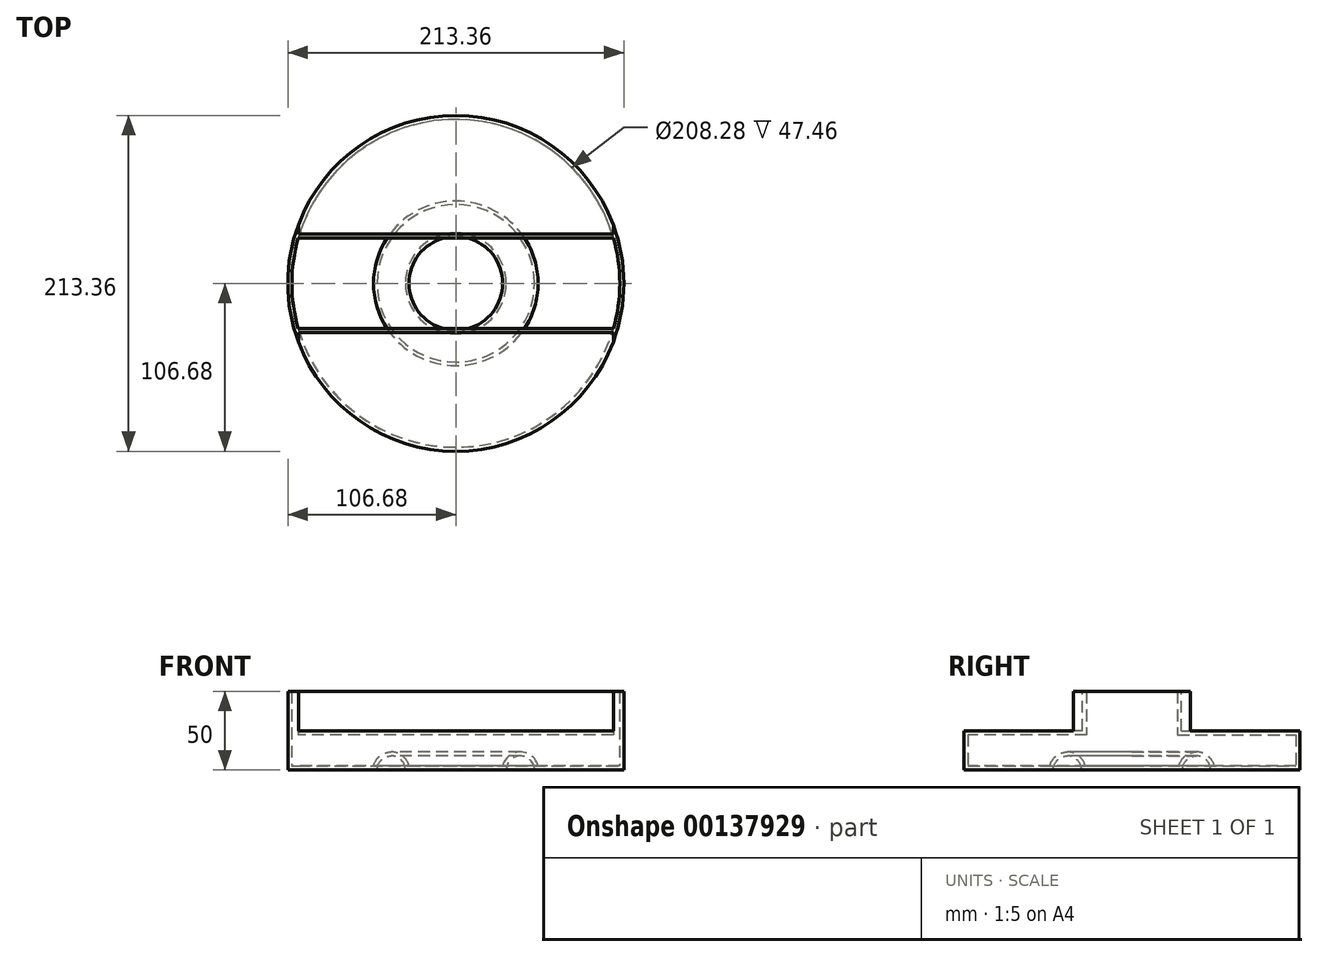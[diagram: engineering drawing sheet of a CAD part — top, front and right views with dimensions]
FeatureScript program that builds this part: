
annotation { "Feature Type Name" : "Feature", "Feature Type Description" : "" }
export const myFeature = defineFeature(function(context is Context, id is Id, definition is map)
    precondition{}
    {
        {
            var Q0;
            Q0=qCreatedBy(makeId("Top.planeOp"),FACE);
            var sketch = newSketch(context, id + "F0", { "sketchPlane" : qUnion([Q0])});
            skCircle(sketch, "E0", {"center": v(0, 0) * mm, "radius": 106.68 * mm});
            skSolve(sketch);
        }
        {
            var Q0;
            Q0 = qSketchRegion(id + "F0", true);
            extrude(context, id + "F1", {"entities" : qUnion([Q0]), "depth" : 50 * mm, "offsetDistance" : 25.4 * mm});
        }
        {
            var Q0;
            Q0=qCreatedBy(makeId("Front.planeOp"),FACE);
            var sketch = newSketch(context, id + "F2", { "sketchPlane" : qUnion([Q0])});
            skCircle(sketch, "E1", {"center": v(41, 0) * mm, "radius": 9 * mm});
            skLineSegment(sketch, "E2", {"start": v(0, -32.67) * mm, "end": v(0, 73.82) * mm, "construction": true});
            skSolve(sketch);
        }
        {
            var Q0;
            Q0 = qSketchRegion(id + "F2", true);
            var Q1;
            Q1=sQuery(id+"F2.wireOp",EDGE,"E2");
            revolve(context, id + "F3", {"operationType" : NewBodyOperationType.REMOVE, "surfaceOperationType" : NewSurfaceOperationType.NEW, "entities" : qUnion([Q0]), "axis" : qUnion([Q1]), "revolveType" : RevolveType.FULL, "oppositeDirection" : true});
        }
        {
            var Q0;
            Q0=qCreatedBy(makeId("Right.planeOp"),FACE);
            var sketch = newSketch(context, id + "F4", { "sketchPlane" : qUnion([Q0])});
            skLineSegment(sketch, "E3", {"start": v(0, 79.99) * mm, "end": v(0, -20) * mm, "construction": true});
            skLineSegment(sketch, "E4.MirrorCS", {"start": v(31.35, 25) * mm, "end": v(119.92, 25) * mm});
            skLineSegment(sketch, "E5.top", {"start": v(31.35, 50.53) * mm, "end": v(119.92, 50.53) * mm});
            skLineSegment(sketch, "E5.left", {"start": v(31.35, 25) * mm, "end": v(31.35, 50.53) * mm});
            skLineSegment(sketch, "E5.right", {"start": v(119.92, 25) * mm, "end": v(119.92, 50.53) * mm});
            skLineSegment(sketch, "E6.MirrorCS", {"start": v(-31.35, 25) * mm, "end": v(-31.35, 50.53) * mm});
            skLineSegment(sketch, "E7.MirrorCS", {"start": v(-31.35, 25) * mm, "end": v(-119.92, 25) * mm});
            skLineSegment(sketch, "E8.MirrorCS", {"start": v(-31.35, 50.53) * mm, "end": v(-119.92, 50.53) * mm});
            skLineSegment(sketch, "E9.MirrorCS", {"start": v(-119.92, 25) * mm, "end": v(-119.92, 50.53) * mm});
            skSolve(sketch);
        }
        {
            var Q0;
            Q0 = qSketchRegion(id + "F4", true);
            extrude(context, id + "F5", {"entities" : qUnion([Q0]), "operationType" : NewBodyOperationType.REMOVE, "endBound" : BoundingType.SYMMETRIC, "depth" : 200 * mm, "offsetDistance" : 25.4 * mm});
        }
        {
            var Q0;
            Q0=makeQuery(id+"F1.opExtrude","CAP_FACE",FACE,{"disambiguationData":[OSD([sQuery(id+"F0.wireOp",EDGE,"E0")])],"isStart":false});
            shell(context, id + "F6", {"entities" : qUnion([Q0]), "thickness" : 2.54 * mm});
        }
    });
